# Revit family: Hand_Dryer-World_Dryer-VMax
name_source: partatom
category: Specialty Equipment
revit_build: Autodesk Revit Architecture 2015 (Build: 20140606_1530(x64)
units: mm (PartAtom-declared; Revit-internal decimal feet)

## types (1)
- VMax
    Apparent Load = 1200 VA
    CFM = 85 CFM
    Cover Finish = Metal - World Dryer - High Impact ABS resin - Silver
    Depth = 0' - 9 1/4"
    Description = Vertical Style High Speed Hand Dryer
    Frequency = 60 Hz
    Height = 2' - 2 1/4"
    Manufacturer = World Dryer
    Model = VMax
    Number of Poles = 1
    Phase = 1
    Power Factor = 1
    Product Documentation Link = http://worlddryer.com
    Product Name = VMax
    Product Page URL = http://worlddryer.com
    Product data url = https://bimobject.com
    RPM = 35000 FPM
    URL = http://worlddryer.com
    Voltage = 120 V
    Watts = 1200 W
    Width = 1' - 1"

## geometry (parser evidence)
native form markers: Blend x7, Sweep x9
no freeform markers — native parametric forms only
